# Revit family: LHBV24
name_source: partatom
category: Lighting Fixtures
units: mm (PartAtom-declared; Revit-internal decimal feet)

## family parameters
Always vertical = Yes
Cut with Voids When Loaded = No
Host = Ceiling
Light Source = Yes
OmniClass Number = 23.80.70.11
OmniClass Title = Luminaries for Internal Lighting
Part Type = Normal
Room Calculation Point = No
Round Connector Dimension = Use Diameter
Shared = No

## types (5) — shared parameters
Assembly Code = D5020200
Color Filter = 16777215
Description = LED High Bay Vapour
Dimming Lamp Color Temperature Shift = <None>
Housing Finish = Metal - Viscor - White
Lamp = LED
Lens Finsih = Acrylic - Viscor - High Impact Textured
Manufacturer = VISIONEERING by VISCOR
Model = LHBV
Tilt Angle = 90.00°
URL = https://www.viscor.com
Voltage = 120 V
Width = 1' - 2 9/16"

## per-type parameters (varying)
| type | Apparent Load | Emit from Line Length | Lamp Wattage | Length | Photometric Web File |
| LHBV24-LED840K080LUNV | 56 VA | 4' - 3 31/32" | 56 VA | 4' - 3 31/32" | LHBV24-LED840K080LUNV-P05.ies |
| LHBV24-LED840K120LUNV | 84 VA | 4' - 3 31/32" | 84 VA | 4' - 3 31/32" | LHBV24-LED840K120LUNV-P05.ies |
| LHBV24-LED840K150LUNV | 106 VA | 4' - 3 31/32" | 106 VA | 4' - 3 31/32" | LHBV24-LED840K150LUNV-P05.ies |
| LHBV24-LED840K180LUNV | 158 VA | 4' - 3 31/32" | 158 VA | 4' - 3 31/32" | LHBV24-LED840K180LUNV-P05.ies |
| LHBV24-LED840K240LUNV | 166 VA | 2' - 2 5/8" | 166 VA | 2' - 2 5/8" |  |

## geometry (parser evidence)
native form markers: Sweep x2
no freeform markers — native parametric forms only
